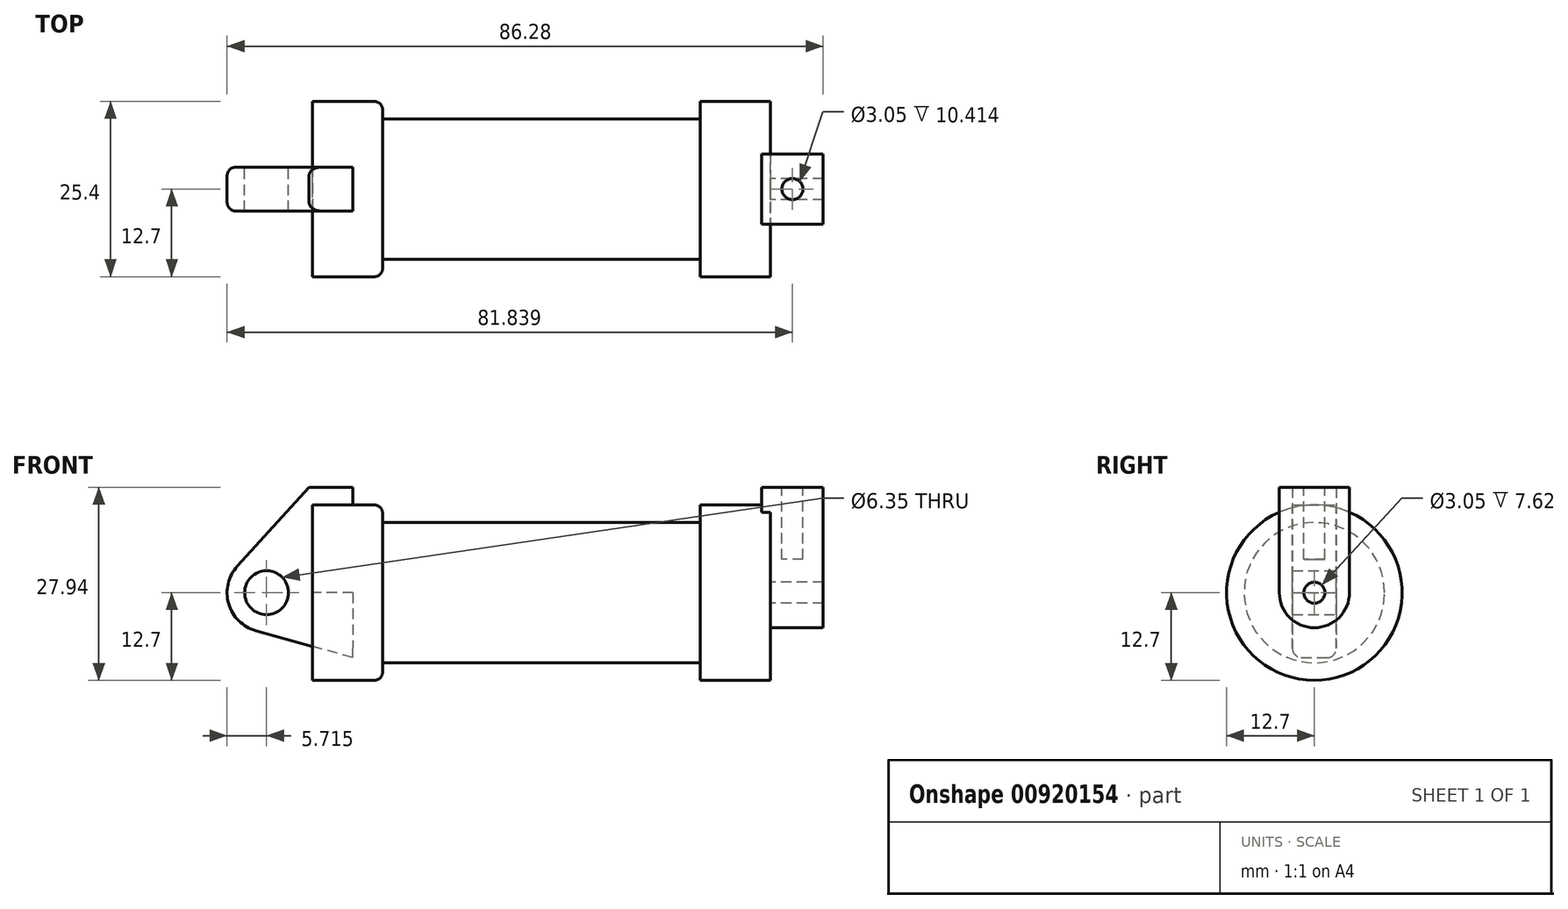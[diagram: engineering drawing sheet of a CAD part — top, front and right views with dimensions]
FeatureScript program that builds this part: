
annotation { "Feature Type Name" : "Feature", "Feature Type Description" : "" }
export const myFeature = defineFeature(function(context is Context, id is Id, definition is map)
    precondition{}
    {
        {
            var Q0;
            Q0=qCreatedBy(makeId("Front.planeOp"),FACE);
            var sketch = newSketch(context, id + "F0", { "sketchPlane" : qUnion([Q0])});
            skLineSegment(sketch, "E0", {"start": v(0, 0) * mm, "end": v(0, 12.7) * mm});
            skLineSegment(sketch, "E1", {"start": v(0, 12.7) * mm, "end": v(10.16, 12.7) * mm});
            skLineSegment(sketch, "E2", {"start": v(10.16, 12.7) * mm, "end": v(10.16, 10.16) * mm});
            skLineSegment(sketch, "E3", {"start": v(10.16, 10.16) * mm, "end": v(56.13, 10.16) * mm});
            skLineSegment(sketch, "E4", {"start": v(56.13, 10.16) * mm, "end": v(56.13, 12.7) * mm});
            skLineSegment(sketch, "E5", {"start": v(56.13, 12.7) * mm, "end": v(66.3, 12.7) * mm});
            skLineSegment(sketch, "E6", {"start": v(66.3, 12.7) * mm, "end": v(66.3, 0) * mm});
            skLineSegment(sketch, "E7", {"start": v(66.3, 0) * mm, "end": v(0, 0) * mm});
            skLineSegment(sketch, "E8", {"start": v(5.84, 15.24) * mm, "end": v(-0.5, 15.24) * mm});
            skLineSegment(sketch, "E9", {"start": v(-0.5, 15.24) * mm, "end": v(-10.88, 3.85) * mm});
            skLineSegment(sketch, "E10", {"start": v(0, 0) * mm, "end": v(-6.65, 0) * mm});
            skCircle(sketch, "E11", {"center": v(-6.65, 0) * mm, "radius": 5.72 * mm});
            skCircle(sketch, "E12", {"center": v(-6.65, 0) * mm, "radius": 3.18 * mm});
            skLineSegment(sketch, "E13", {"start": v(5.84, 15.24) * mm, "end": v(5.84, -9.4) * mm});
            skLineSegment(sketch, "E14", {"start": v(5.84, -9.4) * mm, "end": v(-8.18, -5.5) * mm});
            skSolve(sketch);
        }
        {
            var Q0;
            {var subQ0=sQuery(id+"F0.wireOp",EDGE,"E2");Q0=makeQuery(id+"F0.imprint","IMPRINT",FACE,{"disambiguationData":[TD([[makeQuery(id+"F0.imprint","IMPRINT",EDGE,{"derivedFrom":subQ0}),-1.0]])]});}
            var Q1;
            {var subQ0=sQuery(id+"F0.wireOp",EDGE,"E0");Q1=makeQuery(id+"F0.imprint","IMPRINT",FACE,{"disambiguationData":[TD([[makeQuery(id+"F0.imprint","IMPRINT",EDGE,{"derivedFrom":subQ0}),-1.0]])]});}
            var Q2;
            Q2=sQuery(id+"F0.wireOp",EDGE,"E7");
            revolve(context, id + "F1", {"surfaceOperationType" : NewSurfaceOperationType.NEW, "entities" : qUnion([Q0, Q1]), "axis" : qUnion([Q2]), "revolveType" : RevolveType.FULL});
        }
        {
            var Q0;
            {var subQ1=sQuery(id+"F0.wireOp",EDGE,"E0");Q0=makeQuery(id+"F0.imprint","IMPRINT",FACE,{"disambiguationData":[TD([[makeQuery(id+"F0.imprint","IMPRINT",EDGE,{"derivedFrom":subQ1}),1.0]])]});}
            var Q1;
            {var subQ5=sQuery(id+"F0.wireOp",EDGE,"E12");Q1=makeQuery(id+"F0.imprint","IMPRINT",FACE,{"disambiguationData":[TD([[makeQuery(id+"F0.imprint","IMPRINT",EDGE,{"derivedFrom":subQ5}),-1.0]])]});}
            var Q2;
            {var subQ0=sQuery(id+"F0.wireOp",EDGE,"E14");Q2=makeQuery(id+"F0.imprint","IMPRINT",FACE,{"disambiguationData":[TD([[makeQuery(id+"F0.imprint","IMPRINT",EDGE,{"derivedFrom":subQ0}),-1.0]])]});}
            extrude(context, id + "F2", {"entities" : qUnion([Q0, Q1, Q2]), "endBound" : BoundingType.SYMMETRIC, "depth" : 6.35 * mm, "offsetDistance" : 25.4 * mm});
        }
        {
            var Q0;
            Q0=makeQuery(id+"F1.opRevolve","SWEPT_FACE",FACE,{"disambiguationData":[OSD([sQuery(id+"F0.wireOp",EDGE,"E6")])]});
            var sketch = newSketch(context, id + "F3", { "sketchPlane" : qUnion([Q0])});
            skCircle(sketch, "E15", {"center": v(0, 0) * mm, "radius": 5.08 * mm});
            skCircle(sketch, "E16", {"center": v(0, 0) * mm, "radius": 1.52 * mm});
            skLineSegment(sketch, "E17", {"start": v(-3.22, 15.24) * mm, "end": v(-20.13, 15.24) * mm, "construction": true});
            skLineSegment(sketch, "E18", {"start": v(3.15, 15.24) * mm, "end": v(15.94, 15.24) * mm, "construction": true});
            skLineSegment(sketch, "E19", {"start": v(-5.08, 0) * mm, "end": v(-5.08, 15.24) * mm});
            skLineSegment(sketch, "E20", {"start": v(5.08, 0) * mm, "end": v(5.08, 15.24) * mm});
            skLineSegment(sketch, "E21", {"start": v(-5.08, 15.24) * mm, "end": v(5.08, 15.24) * mm});
            skSolve(sketch);
        }
        {
            var Q0;
            Q0 = qSketchRegion(id + "F3", true);
            extrude(context, id + "F4", {"entities" : qUnion([Q0]), "operationType" : NewBodyOperationType.ADD, "depth" : 7.62 * mm, "offsetDistance" : 25.4 * mm, "hasSecondDirection" : true, "secondDirectionOppositeDirection" : true, "secondDirectionDepth" : 1.27 * mm});
        }
        {
            var Q0;
            Q0=makeQuery(id+"F4.opExtrude","SWEPT_FACE",FACE,{"disambiguationData":[OSD([sQuery(id+"F3.wireOp",EDGE,"E21")])]});
            var sketch = newSketch(context, id + "F5", { "sketchPlane" : qUnion([Q0])});
            skLineSegment(sketch, "E22", {"start": v(66.57, 0) * mm, "end": v(78.17, 0) * mm, "construction": true});
            skPoint(sketch, "E22.startSnap0", {"position": v(65.02, 0) * mm});
            skLineSegment(sketch, "E23", {"start": v(69.47, -5.08) * mm, "end": v(69.47, 7.58) * mm, "construction": true});
            skCircle(sketch, "E24", {"center": v(69.47, 0) * mm, "radius": 1.52 * mm});
            skPoint(sketch, "E24.centerSnap0", {"position": v(69.47, 1.25) * mm});
            skSolve(sketch);
        }
        {
            var Q0;
            Q0=makeQuery(id+"F5.imprint","IMPRINT",FACE,{"disambiguationData":[TD([[makeQuery(id+"F5.imprint","IMPRINT",EDGE,{"derivedFrom":sQuery(id+"F5.wireOp",EDGE,"E24")}),1.0]])]});
            var Q1;
            Q1=sQuery(id+"F5.wireOp",EDGE,"E24");
            extrude(context, id + "F6", {"entities" : qUnion([Q0]), "operationType" : NewBodyOperationType.REMOVE, "surfaceEntities" : qUnion([Q1]), "oppositeDirection" : true, "depth" : 10.4 * mm, "offsetDistance" : 25.4 * mm});
        }
        {
            var Q0;
            Q0=makeQuery(id+"F4.opExtrude","SWEPT_FACE",FACE,{"disambiguationData":[OSD([sQuery(id+"F3.wireOp",EDGE,"E21")])]});
            var Q1;
            Q1=makeQuery(id+"F4.boolean.opBoolean","SPLIT",FACE,{"disambiguationData":[TD([makeQuery(id+"F1.opRevolve","SWEPT_FACE",FACE,{"disambiguationData":[OSD([sQuery(id+"F0.wireOp",EDGE,"E5")])]})])],"derivedFrom":makeQuery(id+"F1.opRevolve","SWEPT_FACE",FACE,{"disambiguationData":[OSD([sQuery(id+"F0.wireOp",EDGE,"E6")])]})});
            var Q2;
            Q2=makeQuery(id+"F4.opExtrude","CAP_FACE",FACE,{"disambiguationData":[OSD([sQuery(id+"F3.wireOp",EDGE,"E15"),sQuery(id+"F3.wireOp",EDGE,"E16"),sQuery(id+"F3.wireOp",EDGE,"E19"),sQuery(id+"F3.wireOp",EDGE,"E20"),sQuery(id+"F3.wireOp",EDGE,"E21")])],"isStart":false});
            var Q3;
            Q3=makeQuery(id+"F1.opRevolve","SWEPT_EDGE",EDGE,{"disambiguationData":[OSD([sQuery(id+"F0.wireOp",EDGE,"E4"),sQuery(id+"F0.wireOp",EDGE,"E5")])]});
            var Q4;
            Q4=makeQuery(id+"F1.opRevolve","SWEPT_EDGE",EDGE,{"disambiguationData":[OSD([sQuery(id+"F0.wireOp",EDGE,"E0"),sQuery(id+"F0.wireOp",EDGE,"E1")])]});
            var Q5;
            Q5=makeQuery(id+"F2.opExtrude","CAP_EDGE",EDGE,{"disambiguationData":[OSD([sQuery(id+"F0.wireOp",EDGE,"E9")])],"isStart":false});
            var Q6;
            Q6=makeQuery(id+"F2.opExtrude","CAP_EDGE",EDGE,{"disambiguationData":[OSD([sQuery(id+"F0.wireOp",EDGE,"E14")])],"isStart":true});
            var Q7;
            Q7=makeQuery(id+"F2.opExtrude","CAP_EDGE",EDGE,{"disambiguationData":[OSD([sQuery(id+"F0.wireOp",EDGE,"E11")])],"isStart":true});
            fillet(context, id + "F7", {"entities" : qUnion([Q0, Q1, Q2, Q3, Q4, Q5, Q6, Q7]), "radius" : 1.27 * mm, "tangentPropagation" : true, "allowEdgeOverflow" : false});
        }
        {
            var Q0;
            Q0=makeQuery(id+"F1.opRevolve","SWEPT_EDGE",EDGE,{"disambiguationData":[OSD([sQuery(id+"F0.wireOp",EDGE,"E1"),sQuery(id+"F0.wireOp",EDGE,"E2")])]});
            fillet(context, id + "F8", {"entities" : qUnion([Q0]), "radius" : 1.27 * mm, "tangentPropagation" : true, "allowEdgeOverflow" : false});
        }
    });
